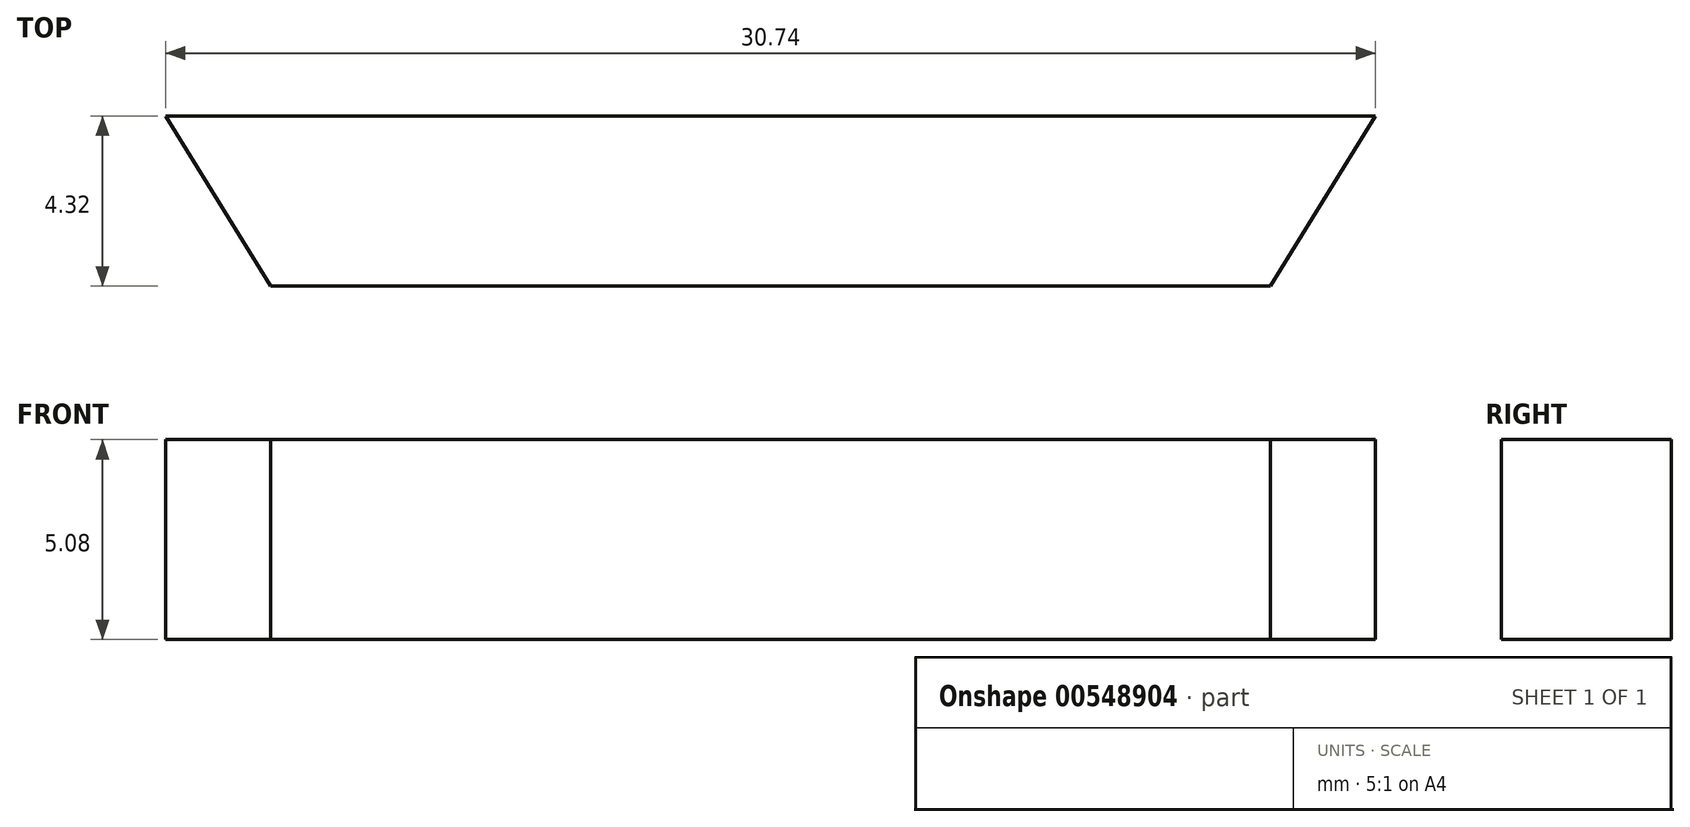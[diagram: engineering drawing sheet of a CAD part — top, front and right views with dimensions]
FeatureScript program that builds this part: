
annotation { "Feature Type Name" : "Feature", "Feature Type Description" : "" }
export const myFeature = defineFeature(function(context is Context, id is Id, definition is map)
    precondition{}
    {
        {
            var Q0;
            Q0=qCreatedBy(makeId("Top.planeOp"),FACE);
            var sketch = newSketch(context, id + "F0", { "sketchPlane" : qUnion([Q0])});
            skLineSegment(sketch, "E0", {"start": v(0, 0) * mm, "end": v(-15.37, 0) * mm});
            skLineSegment(sketch, "E1", {"start": v(0, 0) * mm, "end": v(15.37, 0) * mm});
            skLineSegment(sketch, "E2", {"start": v(-15.37, 0) * mm, "end": v(-12.7, -4.32) * mm});
            skLineSegment(sketch, "E3", {"start": v(15.37, 0) * mm, "end": v(12.7, -4.32) * mm});
            skLineSegment(sketch, "E4", {"start": v(-12.7, -4.32) * mm, "end": v(12.7, -4.32) * mm});
            skSolve(sketch);
        }
        {
            var Q0;
            Q0=makeQuery(id+"F0.imprint","IMPRINT",FACE,{"disambiguationData":[TD([[makeQuery(id+"F0.imprint","IMPRINT",EDGE,{"derivedFrom":sQuery(id+"F0.wireOp",EDGE,"E0")}),1.0]])]});
            extrude(context, id + "F1", {"entities" : qUnion([Q0]), "depth" : 5.08 * mm, "offsetDistance" : 25.4 * mm});
        }
    });
